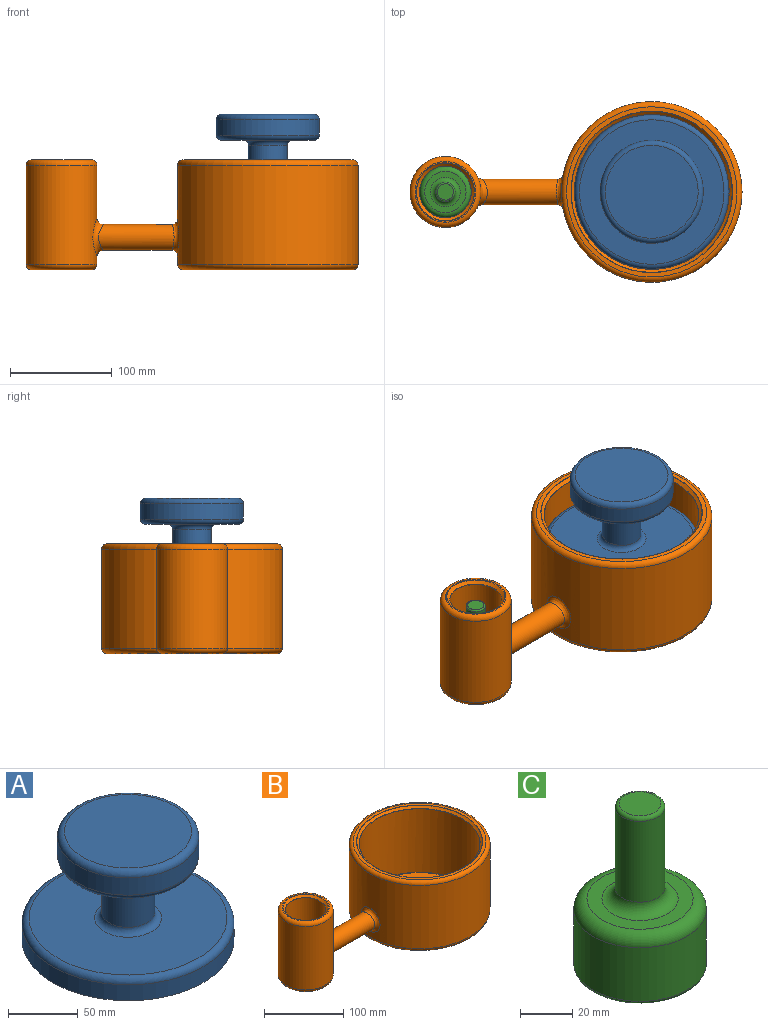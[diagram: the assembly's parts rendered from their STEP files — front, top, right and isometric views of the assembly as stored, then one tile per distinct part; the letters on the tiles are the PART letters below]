
ASSEMBLY  parts=3 mates=2
PART A: 12 faces, bbox 165x165x95.3 mm
  f0: cylinder r=19.05mm len=40.64mm, axis (0,0,-1), area 4864.4mm2, adj f4,f9
  f1: cylinder r=76.2mm len=152.4mm, axis (0,0,1), area 6688.5mm2, adj f2,f5
  f2: plane 152.4x152.4mm, normal (0,0,-1), area 18241.5mm2, adj f1
  f3: plane 142.24x142.24mm, normal (0,0,1), area 14061.1mm2, adj f4,f5
  f4: torus R=24.13mm, axis (0,0,1), area 1047.7mm2, adj f0,f3
  f5: torus R=71.12mm, axis (0,0,1), area 3727.9mm2, adj f1,f3
  f6: cylinder r=50.8mm len=101.6mm, axis (0,0,1), area 4864.4mm2, adj f10,f11
  f7: plane 91.44x91.44mm, normal (0,0,-1), area 4737.7mm2, adj f9,f11
  f8: plane 91.44x91.44mm, normal (0,0,1), area 6566.9mm2, adj f10
  f9: torus R=24.13mm, axis (0,0,1), area 1047.7mm2, adj f0,f7
  f10: torus R=45.72mm, axis (0,0,1), area 2454.4mm2, adj f6,f8
  f11: torus R=45.72mm, axis (0,0,1), area 2454.4mm2, adj f6,f7
PART B: 28 faces, bbox 337.2x192.4x108 mm
  f0: cylinder r=25.4mm len=97.89mm, axis (0,0,1), area 15045.5mm2, adj f11,f23,f27
  f1: cylinder r=34.92mm len=97.79mm, axis (0,0,1), area 20465.5mm2, adj f4,f17,f19
  f2: plane 59.69x59.69mm, normal (0,0,1), area 204.7mm2, adj f19,f22
  f3: cylinder r=12.7mm len=74.3mm, axis (-1,0,0), area 5672.4mm2, adj f4,f9
  f4: bspline ~38.11x32.25mm, area 775.7mm2, adj f1,f3
  f5: plane 167.64x167.64mm, normal (0,0,1), area 2200.1mm2, adj f18,f24
  f6: cylinder r=88.9mm len=177.8mm, axis (0,0,1), area 53680.9mm2, adj f9,f16,f18
  f7: cylinder r=76.2mm len=152.4mm, axis (0,0,1), area 46234.7mm2, adj f10,f25,f26
  f8: cylinder r=9.53mm len=96.49mm, axis (-1,0,0), area 5621.6mm2, adj f10,f11
  f9: bspline ~35.57x33.65mm, area 677.5mm2, adj f3,f6
  f10: bspline ~29.21x27.39mm, area 529.6mm2, adj f7,f8
  f11: bspline ~29.24x24.37mm, area 465.3mm2, adj f0,f8
  f12: plane 50.04x50.04mm, normal (0,0,1), area 1966.5mm2, adj f27
  f13: plane 59.69x59.69mm, normal (0,0,-1), area 2798.3mm2, adj f17
  f14: plane 151.64x151.64mm, normal (0,0,1), area 18059.5mm2, adj f26
  f15: plane 167.64x167.64mm, normal (0,0,-1), area 22072.2mm2, adj f16
  f16: torus R=83.82mm, axis (0,0,1), area 4364.7mm2, adj f6,f15
  f17: torus R=29.84mm, axis (0,0,1), area 1658.5mm2, adj f1,f13
  f18: torus R=83.82mm, axis (0,0,1), area 4364.7mm2, adj f5,f6
  f19: torus R=29.84mm, axis (0,0,1), area 1658.5mm2, adj f1,f2
  f20: cone r=76.2mm half-angle=45deg, axis (0,0,1), area 2040.3mm2, adj f24,f25
  f21: cone r=25.4mm half-angle=45deg, axis (0,0,1), area 707.9mm2, adj f22,f23
  f22: torus R=28.73mm, axis (0,0,1), area 53.8mm2, adj f2,f21
  f23: torus R=25.78mm, axis (0,0,-1), area 47.8mm2, adj f0,f21
  f24: torus R=79.53mm, axis (0,0,1), area 149.3mm2, adj f5,f20
  f25: torus R=76.58mm, axis (0,0,-1), area 143.3mm2, adj f7,f20
  f26: torus R=75.82mm, axis (0,0,1), area 286mm2, adj f7,f14
  f27: torus R=25.02mm, axis (0,0,1), area 95mm2, adj f0,f12
PART C: 9 faces, bbox 55x55x76.2 mm
  f0: cylinder r=25.4mm len=50.8mm, axis (0,0,-1), area 4013.1mm2, adj f6,f8
  f1: plane 40.64x40.64mm, normal (0,0,1), area 627.1mm2, adj f5,f6
  f2: plane 47.75x47.75mm, normal (0,0,-1), area 1790.9mm2, adj f8
  f3: cylinder r=9.53mm len=37.85mm, axis (0,0,-1), area 2265mm2, adj f5,f7
  f4: plane 16x16mm, normal (0,0,1), area 201.1mm2, adj f7
  f5: torus R=14.61mm, axis (0,0,1), area 570.1mm2, adj f1,f3
  f6: torus R=20.32mm, axis (0,0,1), area 1180.9mm2, adj f0,f1
  f7: torus R=8mm, axis (0,0,1), area 134.9mm2, adj f3,f4
  f8: torus R=23.88mm, axis (0,0,1), area 373.7mm2, adj f0,f2
PLACE A rot(axis=(0,0,1),90deg) t=(378.25,22.63,-57.28)mm
PLACE B t=(175.05,22.63,-25.97)mm fixed
PLACE C t=(175.05,22.63,-112.44)mm
MATE slider C.f0 <-> B.f1  axis (0,0,-1) through (175.05,22.63,-112.44)mm
MATE slider A.f1 <-> B.f6  axis (0,0,-1) through (378.25,22.63,-76.33)mm
